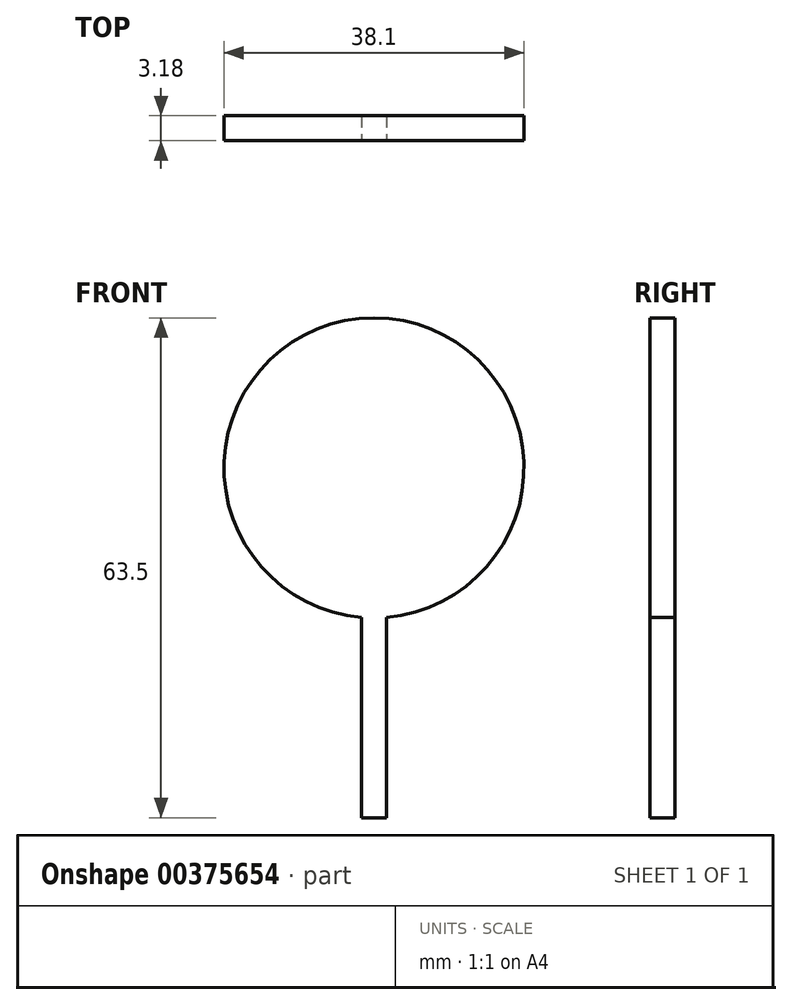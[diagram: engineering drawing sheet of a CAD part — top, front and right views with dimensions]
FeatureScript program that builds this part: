
annotation { "Feature Type Name" : "Feature", "Feature Type Description" : "" }
export const myFeature = defineFeature(function(context is Context, id is Id, definition is map)
    precondition{}
    {
        {
            var Q0;
            Q0=qCreatedBy(makeId("Front.planeOp"),FACE);
            var sketch = newSketch(context, id + "F0", { "sketchPlane" : qUnion([Q0])});
            skLineSegment(sketch, "E0.bottom", {"start": v(44.45, -44.45) * mm, "end": v(-44.45, -44.45) * mm});
            skLineSegment(sketch, "E0.top", {"start": v(44.45, 44.45) * mm, "end": v(-44.45, 44.45) * mm});
            skLineSegment(sketch, "E0.left", {"start": v(44.45, -44.45) * mm, "end": v(44.45, 44.45) * mm});
            skLineSegment(sketch, "E0.right", {"start": v(-44.45, -44.45) * mm, "end": v(-44.45, 44.45) * mm});
            skPoint(sketch, "E0.middle", {"position": v(0, 0) * mm});
            skSolve(sketch);
        }
        {
            var Q0;
            Q0 = qSketchRegion(id + "F0", true);
            extrude(context, id + "F1", {"entities" : qUnion([Q0]), "depth" : 3.17 * mm});
        }
        {
            var Q0;
            Q0=makeQuery(id+"F1.opExtrude","CAP_FACE",FACE,{"disambiguationData":[OSD([sQuery(id+"F0.wireOp",EDGE,"E0.bottom"),sQuery(id+"F0.wireOp",EDGE,"E0.top"),sQuery(id+"F0.wireOp",EDGE,"E0.left"),sQuery(id+"F0.wireOp",EDGE,"E0.right")])],"isStart":false});
            var sketch = newSketch(context, id + "F2", { "sketchPlane" : qUnion([Q0])});
            skArc(sketch, "E1", {"start": v(-1.57, -18.98) * mm, "mid": v(0, 19.05) * mm, "end": v(1.57, -18.98) * mm});
            skLineSegment(sketch, "E2", {"start": v(-1.57, -18.98) * mm, "end": v(-1.57, -44.45) * mm});
            skLineSegment(sketch, "E3", {"start": v(-1.57, -44.45) * mm, "end": v(1.57, -44.45) * mm});
            skLineSegment(sketch, "E4", {"start": v(1.57, -18.98) * mm, "end": v(1.57, -44.45) * mm});
            skSolve(sketch);
        }
        {
            var Q0;
            Q0=makeQuery(id+"F2.imprint","IMPRINT",FACE,{"disambiguationData":[TD([[makeQuery(id+"F2.imprint","IMPRINT",EDGE,{"derivedFrom":sQuery(id+"F2.wireOp",EDGE,"E1")}),-1.0]])]});
            extrude(context, id + "F3", {"entities" : qUnion([Q0]), "operationType" : NewBodyOperationType.REMOVE, "oppositeDirection" : true, "depth" : 25.4 * mm});
        }
    });
